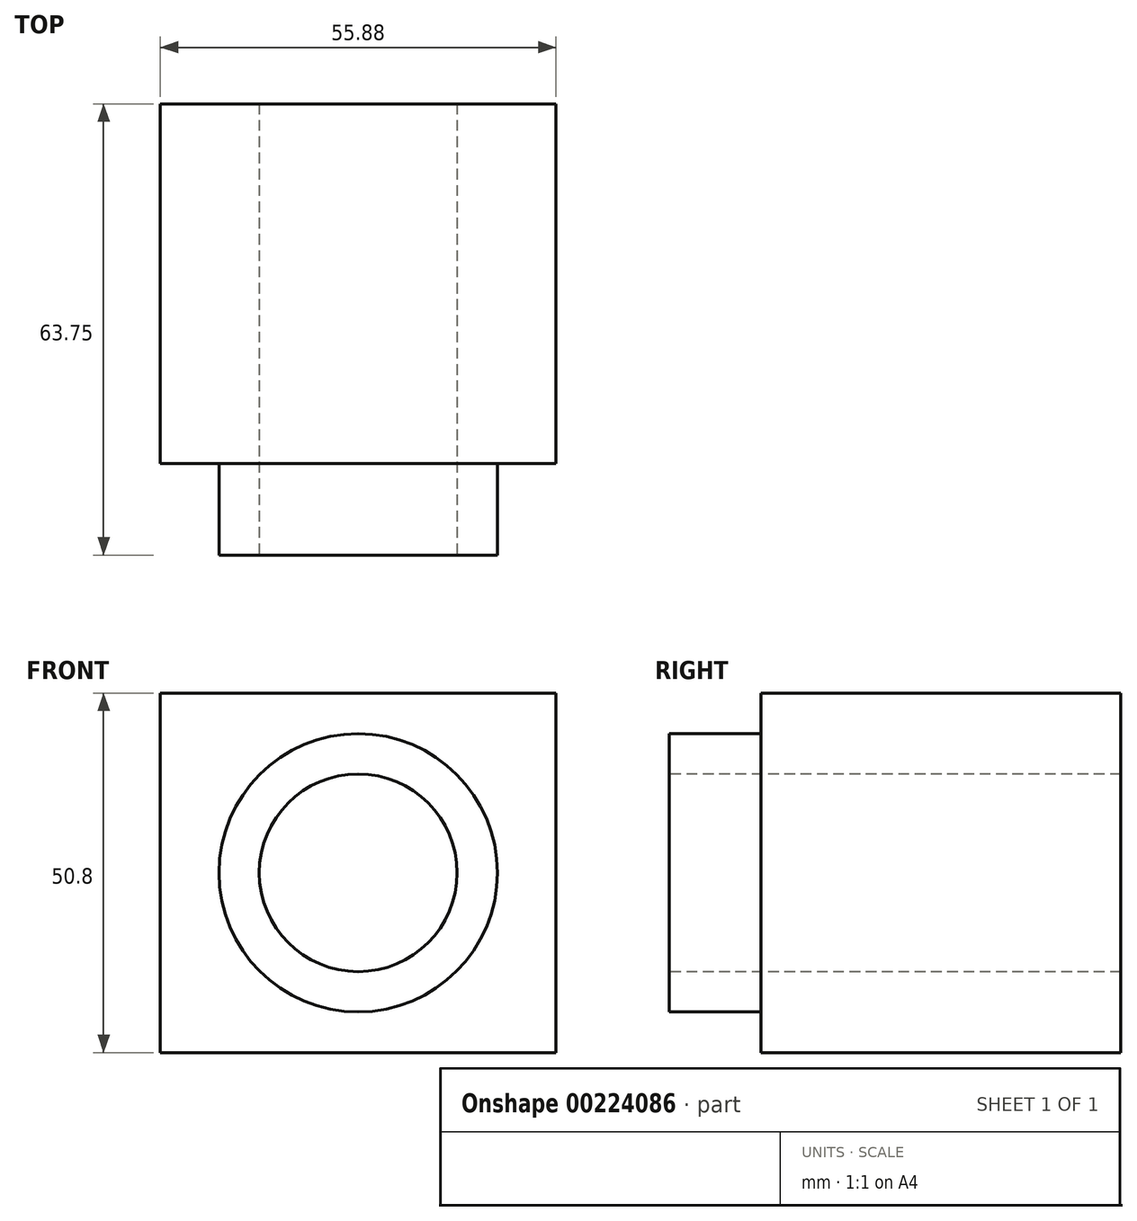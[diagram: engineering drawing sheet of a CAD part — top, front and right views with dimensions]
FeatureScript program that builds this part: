
annotation { "Feature Type Name" : "Feature", "Feature Type Description" : "" }
export const myFeature = defineFeature(function(context is Context, id is Id, definition is map)
    precondition{}
    {
        {
            var Q0;
            Q0=qCreatedBy(makeId("Front.planeOp"),FACE);
            var sketch = newSketch(context, id + "F0", { "sketchPlane" : qUnion([Q0])});
            skLineSegment(sketch, "E0.bottom", {"start": v(27.94, 25.4) * mm, "end": v(-27.94, 25.4) * mm});
            skLineSegment(sketch, "E0.top", {"start": v(27.94, -25.4) * mm, "end": v(-27.94, -25.4) * mm});
            skLineSegment(sketch, "E0.left", {"start": v(27.94, 25.4) * mm, "end": v(27.94, -25.4) * mm});
            skLineSegment(sketch, "E0.right", {"start": v(-27.94, 25.4) * mm, "end": v(-27.94, -25.4) * mm});
            skPoint(sketch, "E0.middle", {"position": v(0, 0) * mm});
            skSolve(sketch);
        }
        {
            var Q0;
            Q0=makeQuery(id+"F0.imprint","IMPRINT",FACE,{"disambiguationData":[TD([[makeQuery(id+"F0.imprint","IMPRINT",EDGE,{"derivedFrom":sQuery(id+"F0.wireOp",EDGE,"E0.bottom")}),1.0]])]});
            extrude(context, id + "F1", {"entities" : qUnion([Q0]), "endBound" : BoundingType.SYMMETRIC, "depth" : 50.8 * mm});
        }
        {
            var Q0;
            Q0=makeQuery(id+"F1.opExtrude","CAP_FACE",FACE,{"disambiguationData":[OSD([sQuery(id+"F0.wireOp",EDGE,"E0.bottom"),sQuery(id+"F0.wireOp",EDGE,"E0.top"),sQuery(id+"F0.wireOp",EDGE,"E0.left"),sQuery(id+"F0.wireOp",EDGE,"E0.right")])],"isStart":false});
            var sketch = newSketch(context, id + "F2", { "sketchPlane" : qUnion([Q0])});
            skCircle(sketch, "E1", {"center": v(0, 0) * mm, "radius": 13.97 * mm});
            skSolve(sketch);
        }
        {
            var Q0;
            Q0 = qSketchRegion(id + "F2", true);
            extrude(context, id + "F3", {"entities" : qUnion([Q0]), "operationType" : NewBodyOperationType.REMOVE, "oppositeDirection" : true, "depth" : 127 * mm});
        }
        {
            var Q0;
            Q0=makeQuery(id+"F1.opExtrude","CAP_FACE",FACE,{"disambiguationData":[OSD([sQuery(id+"F0.wireOp",EDGE,"E0.bottom"),sQuery(id+"F0.wireOp",EDGE,"E0.top"),sQuery(id+"F0.wireOp",EDGE,"E0.left"),sQuery(id+"F0.wireOp",EDGE,"E0.right")])],"isStart":false});
            var sketch = newSketch(context, id + "F4", { "sketchPlane" : qUnion([Q0])});
            skCircle(sketch, "E2", {"center": v(0, 0) * mm, "radius": 19.66 * mm});
            skSolve(sketch);
        }
        {
            var Q0;
            Q0=makeQuery(id+"F4.imprint","IMPRINT",FACE,{"disambiguationData":[TD([[makeQuery(id+"F4.imprint","IMPRINT",EDGE,{"derivedFrom":sQuery(id+"F4.wireOp",EDGE,"E2")}),1.0]])]});
            extrude(context, id + "F5", {"entities" : qUnion([Q0]), "operationType" : NewBodyOperationType.ADD, "depth" : 12.95 * mm});
        }
    });
